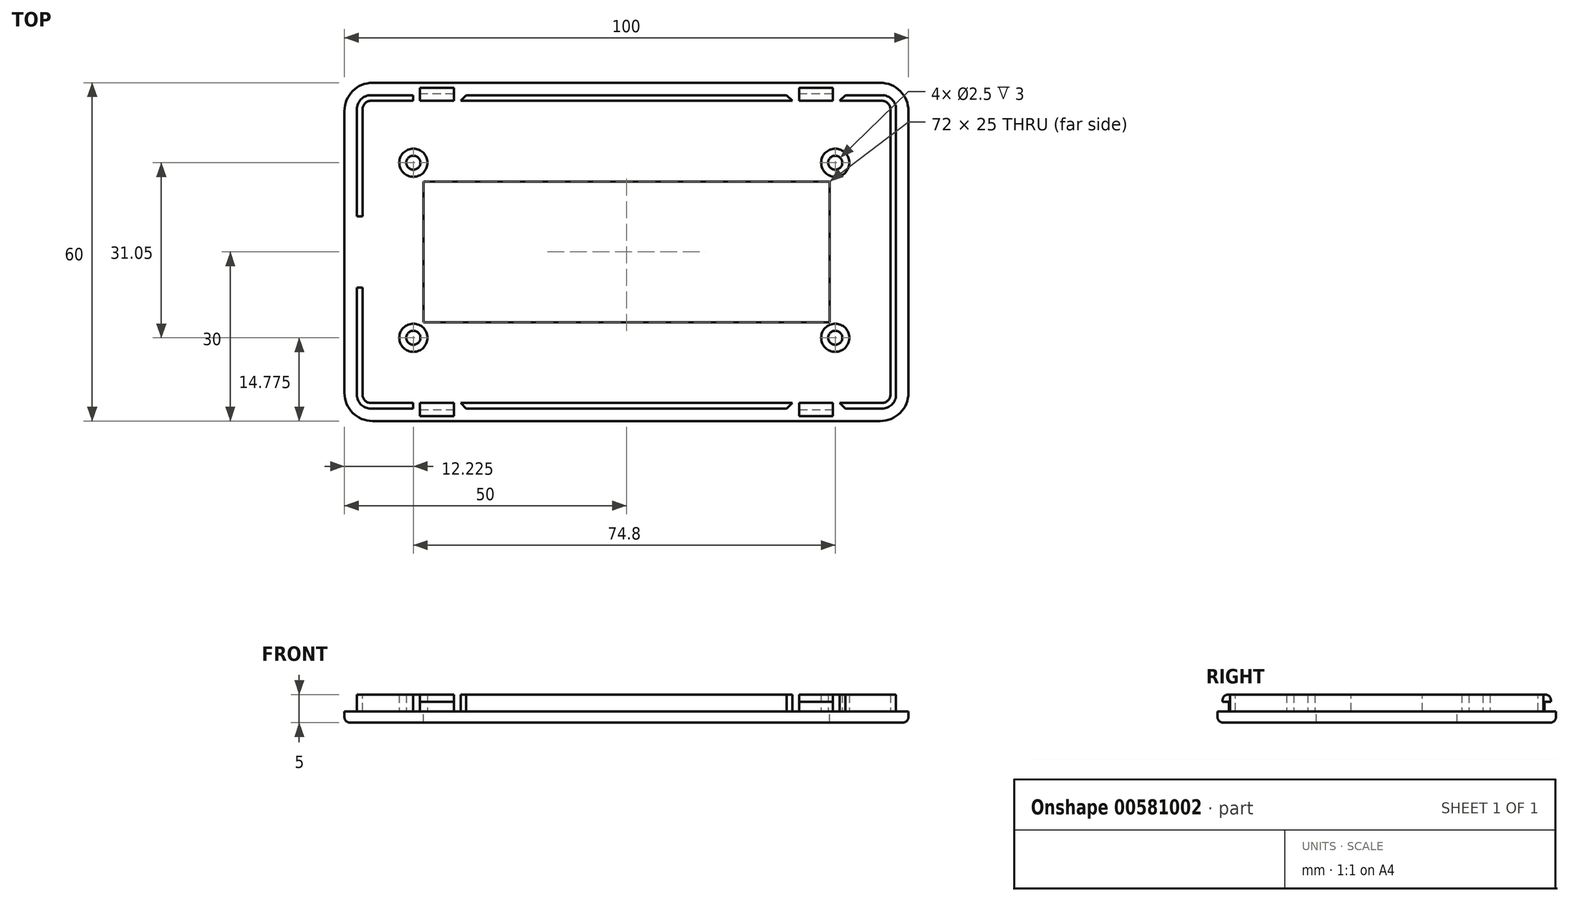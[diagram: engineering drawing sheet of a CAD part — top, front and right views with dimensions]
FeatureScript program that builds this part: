
annotation { "Feature Type Name" : "Feature", "Feature Type Description" : "" }
export const myFeature = defineFeature(function(context is Context, id is Id, definition is map)
    precondition{}
    {
        {
            var Q0;
            Q0=qCreatedBy(makeId("Top.planeOp"),FACE);
            var sketch = newSketch(context, id + "F0", { "sketchPlane" : qUnion([Q0])});
            skLineSegment(sketch, "E0.bottom", {"start": v(5, 0) * mm, "end": v(95, 0) * mm});
            skLineSegment(sketch, "E0.left", {"start": v(0, 5) * mm, "end": v(0, 30) * mm});
            skLineSegment(sketch, "E0.right", {"start": v(100, 5) * mm, "end": v(100, 30) * mm});
            skLineSegment(sketch, "E1.top", {"start": v(4.7, 2.2) * mm, "end": v(95.3, 2.2) * mm});
            skLineSegment(sketch, "E1.left", {"start": v(2.2, 30) * mm, "end": v(2.2, 4.7) * mm});
            skLineSegment(sketch, "E1.right", {"start": v(97.8, 30) * mm, "end": v(97.8, 4.7) * mm});
            skPoint(sketch, "E2.visualSharp", {"position": v(0, 0) * mm});
            skArc(sketch, "E2.filletArc", {"start": v(0, 5) * mm, "mid": v(1.46, 1.46) * mm, "end": v(5, 0) * mm});
            skPoint(sketch, "E3.visualSharp", {"position": v(100, 0) * mm});
            skArc(sketch, "E3.filletArc", {"start": v(95, 0) * mm, "mid": v(98.54, 1.46) * mm, "end": v(100, 5) * mm});
            skPoint(sketch, "E4.visualSharp", {"position": v(97.8, 2.2) * mm});
            skArc(sketch, "E4.filletArc", {"start": v(95.3, 2.2) * mm, "mid": v(97.07, 2.93) * mm, "end": v(97.8, 4.7) * mm});
            skPoint(sketch, "E5.visualSharp", {"position": v(2.2, 2.2) * mm});
            skArc(sketch, "E5.filletArc", {"start": v(2.2, 4.7) * mm, "mid": v(2.93, 2.93) * mm, "end": v(4.7, 2.2) * mm});
            skLineSegment(sketch, "E6.1", {"start": v(3.2, 30) * mm, "end": v(3.2, 4.7) * mm});
            skLineSegment(sketch, "E6.2", {"start": v(4.7, 3.2) * mm, "end": v(95.3, 3.2) * mm});
            skLineSegment(sketch, "E6.3", {"start": v(96.8, 30) * mm, "end": v(96.8, 4.7) * mm});
            skPoint(sketch, "E7.visualSharp", {"position": v(96.8, 3.2) * mm});
            skArc(sketch, "E7.filletArc", {"start": v(95.3, 3.2) * mm, "mid": v(96.36, 3.64) * mm, "end": v(96.8, 4.7) * mm});
            skPoint(sketch, "E8.visualSharp", {"position": v(3.2, 3.2) * mm});
            skArc(sketch, "E8.filletArc", {"start": v(3.2, 4.7) * mm, "mid": v(3.64, 3.64) * mm, "end": v(4.7, 3.2) * mm});
            skLineSegment(sketch, "E9", {"start": v(0, 30) * mm, "end": v(100, 30) * mm});
            skSolve(sketch);
        }
        {
            var Q0;
            Q0 = qSketchRegion(id + "F0", true);
            var Q1;
            Q1=makeQuery(id+"F0.imprint","IMPRINT",FACE,{"disambiguationData":[TD([[makeQuery(id+"F0.imprint","IMPRINT",EDGE,{"derivedFrom":sQuery(id+"F0.wireOp",EDGE,"E6.0")}),-1.0]])]});
            var Q2;
            Q2=makeQuery(id+"F0.imprint","IMPRINT",FACE,{"disambiguationData":[TD([[makeQuery(id+"F0.imprint","IMPRINT",EDGE,{"derivedFrom":sQuery(id+"F0.wireOp",EDGE,"E1.bottom")}),-1.0]])]});
            extrude(context, id + "F1", {"entities" : qUnion([Q0, Q1, Q2]), "depth" : 2 * mm, "offsetDistance" : 25 * mm});
        }
        {
            var Q0;
            Q0=makeQuery(id+"F0.imprint","IMPRINT",FACE,{"disambiguationData":[TD([[makeQuery(id+"F0.imprint","IMPRINT",EDGE,{"derivedFrom":sQuery(id+"F0.wireOp",EDGE,"E1.top")}),1.0]])]});
            extrude(context, id + "F2", {"entities" : qUnion([Q0]), "operationType" : NewBodyOperationType.ADD, "depth" : 5 * mm, "offsetDistance" : 25 * mm});
        }
        {
            var Q0;
            Q0=makeQuery(id+"F2.opExtrude","CAP_FACE",FACE,{"disambiguationData":[OSD([sQuery(id+"F0.wireOp",EDGE,"E1.top"),sQuery(id+"F0.wireOp",EDGE,"E1.left"),sQuery(id+"F0.wireOp",EDGE,"E1.right"),sQuery(id+"F0.wireOp",EDGE,"E4.filletArc"),sQuery(id+"F0.wireOp",EDGE,"E5.filletArc"),sQuery(id+"F0.wireOp",EDGE,"E6.1"),sQuery(id+"F0.wireOp",EDGE,"E6.2"),sQuery(id+"F0.wireOp",EDGE,"E6.3"),sQuery(id+"F0.wireOp",EDGE,"E7.filletArc"),sQuery(id+"F0.wireOp",EDGE,"E8.filletArc"),sQuery(id+"F0.wireOp",EDGE,"E9")])],"isStart":false});
            var sketch = newSketch(context, id + "F3", { "sketchPlane" : qUnion([Q0])});
            skLineSegment(sketch, "E10.bottom", {"start": v(2.2, 30) * mm, "end": v(3.2, 30) * mm});
            skLineSegment(sketch, "E10.top", {"start": v(2.2, 23.7) * mm, "end": v(3.2, 23.7) * mm});
            skLineSegment(sketch, "E10.left", {"start": v(2.2, 30) * mm, "end": v(2.2, 23.7) * mm});
            skLineSegment(sketch, "E10.right", {"start": v(3.2, 30) * mm, "end": v(3.2, 23.7) * mm});
            skLineSegment(sketch, "E11.bottom", {"start": v(12.2, 3.2) * mm, "end": v(13.4, 3.2) * mm});
            skLineSegment(sketch, "E11.top", {"start": v(12.2, 2.2) * mm, "end": v(13.4, 2.2) * mm});
            skLineSegment(sketch, "E11.left", {"start": v(12.2, 3.2) * mm, "end": v(12.2, 2.2) * mm});
            skLineSegment(sketch, "E11.right", {"start": v(13.4, 3.2) * mm, "end": v(13.4, 2.2) * mm});
            skLineSegment(sketch, "E12.bottom", {"start": v(86.6, 3.2) * mm, "end": v(87.8, 3.2) * mm});
            skLineSegment(sketch, "E12.top", {"start": v(86.6, 2.2) * mm, "end": v(87.8, 2.2) * mm});
            skLineSegment(sketch, "E12.left", {"start": v(86.6, 3.2) * mm, "end": v(86.6, 2.2) * mm});
            skLineSegment(sketch, "E12.right", {"start": v(87.8, 3.2) * mm, "end": v(87.8, 2.2) * mm});
            skLineSegment(sketch, "E13.bottom", {"start": v(19.4, 3.2) * mm, "end": v(20.6, 3.2) * mm});
            skLineSegment(sketch, "E13.top", {"start": v(19.4, 2.2) * mm, "end": v(20.6, 2.2) * mm});
            skLineSegment(sketch, "E13.left", {"start": v(19.4, 3.2) * mm, "end": v(19.4, 2.2) * mm});
            skLineSegment(sketch, "E13.right", {"start": v(20.6, 3.2) * mm, "end": v(20.6, 2.2) * mm});
            skLineSegment(sketch, "E14.bottom", {"start": v(80.6, 3.2) * mm, "end": v(79.4, 3.2) * mm});
            skLineSegment(sketch, "E14.top", {"start": v(80.6, 2.2) * mm, "end": v(79.4, 2.2) * mm});
            skLineSegment(sketch, "E14.left", {"start": v(80.6, 3.2) * mm, "end": v(80.6, 2.2) * mm});
            skLineSegment(sketch, "E14.right", {"start": v(79.4, 3.2) * mm, "end": v(79.4, 2.2) * mm});
            skSolve(sketch);
        }
        {
            var Q0;
            Q0=makeQuery(id+"F3.imprint","IMPRINT",FACE,{"disambiguationData":[TD([[makeQuery(id+"F3.imprint","IMPRINT",EDGE,{"derivedFrom":sQuery(id+"F3.wireOp",EDGE,"E10.bottom")}),-1.0]])]});
            var Q1;
            Q1=makeQuery(id+"F3.imprint","IMPRINT",FACE,{"disambiguationData":[TD([[makeQuery(id+"F3.imprint","IMPRINT",EDGE,{"derivedFrom":sQuery(id+"F3.wireOp",EDGE,"E11.bottom")}),-1.0]])]});
            var Q2;
            Q2=makeQuery(id+"F3.imprint","IMPRINT",FACE,{"disambiguationData":[TD([[makeQuery(id+"F3.imprint","IMPRINT",EDGE,{"derivedFrom":sQuery(id+"F3.wireOp",EDGE,"E13.bottom")}),-1.0]])]});
            var Q3;
            Q3=makeQuery(id+"F3.imprint","IMPRINT",FACE,{"disambiguationData":[TD([[makeQuery(id+"F3.imprint","IMPRINT",EDGE,{"derivedFrom":sQuery(id+"F3.wireOp",EDGE,"E14.bottom")}),-1.0]])]});
            var Q4;
            Q4=makeQuery(id+"F3.imprint","IMPRINT",FACE,{"disambiguationData":[TD([[makeQuery(id+"F3.imprint","IMPRINT",EDGE,{"derivedFrom":sQuery(id+"F3.wireOp",EDGE,"E12.bottom")}),-1.0]])]});
            extrude(context, id + "F4", {"entities" : qUnion([Q0, Q1, Q2, Q3, Q4]), "operationType" : NewBodyOperationType.REMOVE, "oppositeDirection" : true, "depth" : 3 * mm, "offsetDistance" : 25 * mm});
        }
        {
            var Q0;
            {var subQ0=sQuery(id+"F3.wireOp",EDGE,"E11.right");var subQ2=sQuery(id+"F0.wireOp",EDGE,"E1.top");Q0=makeQuery(id+"F4.boolean.opBoolean","SPLIT",FACE,{"disambiguationData":[TD([makeQuery(id+"F4.opExtrude","SWEPT_FACE",FACE,{"disambiguationData":[OSD([subQ0])]})])],"derivedFrom":makeQuery(id+"F2.opExtrude","SWEPT_FACE",FACE,{"disambiguationData":[OSD([subQ2])]})});}
            var Q1;
            {var subQ1=sQuery(id+"F0.wireOp",EDGE,"E1.top");var subQ3=sQuery(id+"F3.wireOp",EDGE,"E12.left");Q1=makeQuery(id+"F4.boolean.opBoolean","SPLIT",FACE,{"disambiguationData":[TD([makeQuery(id+"F4.opExtrude","SWEPT_FACE",FACE,{"disambiguationData":[OSD([subQ3])]})])],"derivedFrom":makeQuery(id+"F2.opExtrude","SWEPT_FACE",FACE,{"disambiguationData":[OSD([subQ1])]})});}
            extrude(context, id + "F5", {"entities" : qUnion([Q0, Q1]), "operationType" : NewBodyOperationType.ADD, "depth" : 0.2 * mm, "offsetDistance" : 25 * mm});
        }
        {
            var Q0;
            {var subQ0=sQuery(id+"F3.wireOp",EDGE,"E11.right");var subQ2=sQuery(id+"F0.wireOp",EDGE,"E1.top");Q0=makeQuery(id+"F5.opExtrude","CAP_FACE",FACE,{"disambiguationData":[OSD([subQ2]),TDD([makeQuery(id+"F4.boolean.opBoolean","SPLIT",FACE,{"disambiguationData":[TD([makeQuery(id+"F4.opExtrude","SWEPT_FACE",FACE,{"disambiguationData":[OSD([subQ0])]})])],"derivedFrom":makeQuery(id+"F2.opExtrude","SWEPT_FACE",FACE,{"disambiguationData":[OSD([subQ2])]})})])],"isStart":false});}
            var sketch = newSketch(context, id + "F6", { "sketchPlane" : qUnion([Q0])});
            skLineSegment(sketch, "E15.bottom", {"start": v(13.4, 5) * mm, "end": v(19.4, 5) * mm});
            skLineSegment(sketch, "E15.top", {"start": v(13.4, 3.7) * mm, "end": v(19.4, 3.7) * mm});
            skLineSegment(sketch, "E15.left", {"start": v(13.4, 5) * mm, "end": v(13.4, 3.7) * mm});
            skLineSegment(sketch, "E15.right", {"start": v(19.4, 5) * mm, "end": v(19.4, 3.7) * mm});
            skSolve(sketch);
        }
        {
            var Q0;
            {var subQ1=sQuery(id+"F0.wireOp",EDGE,"E1.top");var subQ3=sQuery(id+"F3.wireOp",EDGE,"E12.left");Q0=makeQuery(id+"F5.opExtrude","CAP_FACE",FACE,{"disambiguationData":[OSD([subQ1]),TDD([makeQuery(id+"F4.boolean.opBoolean","SPLIT",FACE,{"disambiguationData":[TD([makeQuery(id+"F4.opExtrude","SWEPT_FACE",FACE,{"disambiguationData":[OSD([subQ3])]})])],"derivedFrom":makeQuery(id+"F2.opExtrude","SWEPT_FACE",FACE,{"disambiguationData":[OSD([subQ1])]})})])],"isStart":false});}
            var sketch = newSketch(context, id + "F7", { "sketchPlane" : qUnion([Q0])});
            skLineSegment(sketch, "E16.bottom", {"start": v(80.6, 5) * mm, "end": v(86.6, 5) * mm});
            skLineSegment(sketch, "E16.top", {"start": v(80.6, 3.7) * mm, "end": v(86.6, 3.7) * mm});
            skLineSegment(sketch, "E16.left", {"start": v(80.6, 5) * mm, "end": v(80.6, 3.7) * mm});
            skLineSegment(sketch, "E16.right", {"start": v(86.6, 5) * mm, "end": v(86.6, 3.7) * mm});
            skSolve(sketch);
        }
        {
            var Q0;
            Q0=makeQuery(id+"F6.imprint","IMPRINT",FACE,{"disambiguationData":[TD([[makeQuery(id+"F6.imprint","IMPRINT",EDGE,{"derivedFrom":sQuery(id+"F6.wireOp",EDGE,"E15.bottom")}),-1.0]])]});
            var Q1;
            Q1=makeQuery(id+"F7.imprint","IMPRINT",FACE,{"disambiguationData":[TD([[makeQuery(id+"F7.imprint","IMPRINT",EDGE,{"derivedFrom":sQuery(id+"F7.wireOp",EDGE,"E16.bottom")}),-1.0]])]});
            extrude(context, id + "F8", {"entities" : qUnion([Q0, Q1]), "operationType" : NewBodyOperationType.ADD, "depth" : 1.1 * mm, "offsetDistance" : 25 * mm});
        }
        {
            var Q0;
            Q0=makeQuery(id+"F8.opExtrude","CAP_EDGE",EDGE,{"disambiguationData":[OSD([sQuery(id+"F6.wireOp",EDGE,"E15.bottom")])],"isStart":false});
            var Q1;
            Q1=makeQuery(id+"F8.opExtrude","CAP_EDGE",EDGE,{"disambiguationData":[OSD([sQuery(id+"F7.wireOp",EDGE,"E16.bottom")])],"isStart":false});
            fillet(context, id + "F9", {"entities" : qUnion([Q0, Q1]), "radius" : 1 * mm, "tangentPropagation" : true, "allowEdgeOverflow" : false});
        }
        {
            var Q0;
            Q0=makeQuery(id+"F4.boolean.opBoolean","COPY",EDGE,{"derivedFrom":makeQuery(id+"F4.opExtrude","SWEPT_EDGE",EDGE,{"disambiguationData":[OSD([sQuery(id+"F0.wireOp",EDGE,"E1.top"),sQuery(id+"F3.wireOp",EDGE,"E13.top"),sQuery(id+"F3.wireOp",EDGE,"E13.right")])]})});
            var Q1;
            Q1=makeQuery(id+"F4.boolean.opBoolean","COPY",EDGE,{"derivedFrom":makeQuery(id+"F4.opExtrude","SWEPT_EDGE",EDGE,{"disambiguationData":[OSD([sQuery(id+"F0.wireOp",EDGE,"E1.top"),sQuery(id+"F3.wireOp",EDGE,"E11.top"),sQuery(id+"F3.wireOp",EDGE,"E11.left")])]})});
            var Q2;
            Q2=makeQuery(id+"F4.boolean.opBoolean","COPY",EDGE,{"derivedFrom":makeQuery(id+"F4.opExtrude","SWEPT_EDGE",EDGE,{"disambiguationData":[OSD([sQuery(id+"F0.wireOp",EDGE,"E1.top"),sQuery(id+"F3.wireOp",EDGE,"E14.top"),sQuery(id+"F3.wireOp",EDGE,"E14.right")])]})});
            var Q3;
            Q3=makeQuery(id+"F4.boolean.opBoolean","COPY",EDGE,{"derivedFrom":makeQuery(id+"F4.opExtrude","SWEPT_EDGE",EDGE,{"disambiguationData":[OSD([sQuery(id+"F0.wireOp",EDGE,"E1.top"),sQuery(id+"F3.wireOp",EDGE,"E12.top"),sQuery(id+"F3.wireOp",EDGE,"E12.right")])]})});
            var Q4;
            Q4=makeQuery(id+"F4.boolean.opBoolean","COPY",EDGE,{"derivedFrom":makeQuery(id+"F4.opExtrude","SWEPT_EDGE",EDGE,{"disambiguationData":[OSD([sQuery(id+"F0.wireOp",EDGE,"E1.left"),sQuery(id+"F3.wireOp",EDGE,"E10.top"),sQuery(id+"F3.wireOp",EDGE,"E10.left")])]})});
            chamfer(context, id + "F10", {"entities" : qUnion([Q0, Q1, Q2, Q3, Q4]), "width" : 1 * mm, "tangentPropagation" : true});
        }
        {
            var Q0;
            {var subQ2=sQuery(id+"F0.wireOp",EDGE,"E9");var subQ4=sQuery(id+"F0.wireOp",EDGE,"E3.filletArc");var subQ5=sQuery(id+"F0.wireOp",EDGE,"E0.bottom");var subQ6=sQuery(id+"F0.wireOp",EDGE,"E2.filletArc");var subQ7=sQuery(id+"F0.wireOp",EDGE,"E0.left");var subQ8=sQuery(id+"F0.wireOp",EDGE,"E0.right");var subQ9=sQuery(id+"F0.wireOp",EDGE,"E6.1");var subQ13=makeQuery(id+"F1.opExtrude","CAP_FACE",FACE,{"disambiguationData":[OSD([subQ5,subQ7,subQ8,subQ6,subQ4,subQ2])],"isStart":false});Q0=makeQuery(id+"F4.boolean.opBoolean","MERGE",FACE,{"derivedFrom":[makeQuery(id+"F2.boolean.opBoolean","SPLIT",FACE,{"disambiguationData":[TD([makeQuery(id+"F2.opExtrude","SWEPT_FACE",FACE,{"disambiguationData":[OSD([subQ9])]})])],"derivedFrom":subQ13}),makeQuery(id+"F2.boolean.opBoolean","SPLIT",FACE,{"disambiguationData":[TD([makeQuery(id+"F1.opExtrude","SWEPT_FACE",FACE,{"disambiguationData":[OSD([subQ5])]})])],"derivedFrom":subQ13}),makeQuery(id+"F4.opExtrude","CAP_FACE",FACE,{"disambiguationData":[OSD([sQuery(id+"F3.wireOp",EDGE,"E10.bottom"),sQuery(id+"F3.wireOp",EDGE,"E10.top"),sQuery(id+"F3.wireOp",EDGE,"E10.left"),sQuery(id+"F3.wireOp",EDGE,"E10.right")])],"isStart":false}),makeQuery(id+"F4.opExtrude","CAP_FACE",FACE,{"disambiguationData":[OSD([sQuery(id+"F3.wireOp",EDGE,"E11.bottom"),sQuery(id+"F3.wireOp",EDGE,"E11.top"),sQuery(id+"F3.wireOp",EDGE,"E11.left"),sQuery(id+"F3.wireOp",EDGE,"E11.right")])],"isStart":false}),makeQuery(id+"F4.opExtrude","CAP_FACE",FACE,{"disambiguationData":[OSD([sQuery(id+"F3.wireOp",EDGE,"E12.bottom"),sQuery(id+"F3.wireOp",EDGE,"E12.top"),sQuery(id+"F3.wireOp",EDGE,"E12.left"),sQuery(id+"F3.wireOp",EDGE,"E12.right")])],"isStart":false}),makeQuery(id+"F4.opExtrude","CAP_FACE",FACE,{"disambiguationData":[OSD([sQuery(id+"F3.wireOp",EDGE,"E13.bottom"),sQuery(id+"F3.wireOp",EDGE,"E13.top"),sQuery(id+"F3.wireOp",EDGE,"E13.left"),sQuery(id+"F3.wireOp",EDGE,"E13.right")])],"isStart":false}),makeQuery(id+"F4.opExtrude","CAP_FACE",FACE,{"disambiguationData":[OSD([sQuery(id+"F3.wireOp",EDGE,"E14.bottom"),sQuery(id+"F3.wireOp",EDGE,"E14.top"),sQuery(id+"F3.wireOp",EDGE,"E14.left"),sQuery(id+"F3.wireOp",EDGE,"E14.right")])],"isStart":false})]});}
            var sketch = newSketch(context, id + "F11", { "sketchPlane" : qUnion([Q0])});
            skLineSegment(sketch, "E17.bottom", {"start": v(86, 17.5) * mm, "end": v(14, 17.5) * mm});
            skLineSegment(sketch, "E17.top", {"start": v(86, 42.5) * mm, "end": v(14, 42.5) * mm});
            skLineSegment(sketch, "E17.left", {"start": v(86, 17.5) * mm, "end": v(86, 42.5) * mm});
            skLineSegment(sketch, "E17.right", {"start": v(14, 17.5) * mm, "end": v(14, 42.5) * mm});
            skPoint(sketch, "E17.middle", {"position": v(50, 30) * mm});
            skSolve(sketch);
        }
        {
            var Q0;
            {var subQ0=sQuery(id+"F11.wireOp",EDGE,"E17.bottom");Q0=makeQuery(id+"F11.imprint","IMPRINT",FACE,{"disambiguationData":[TD([[makeQuery(id+"F11.imprint","IMPRINT",EDGE,{"derivedFrom":subQ0}),-1.0]])]});}
            extrude(context, id + "F12", {"entities" : qUnion([Q0]), "operationType" : NewBodyOperationType.REMOVE, "endBound" : BoundingType.UP_TO_NEXT, "oppositeDirection" : true, "depth" : 25 * mm, "offsetDistance" : 25 * mm});
        }
        {
            var Q0;
            Q0=makeQuery(id+"F1.opExtrude","CAP_EDGE",EDGE,{"disambiguationData":[OSD([sQuery(id+"F0.wireOp",EDGE,"E0.bottom")])],"isStart":true});
            fillet(context, id + "F13", {"entities" : qUnion([Q0]), "radius" : 1 * mm, "tangentPropagation" : true, "allowEdgeOverflow" : false});
        }
        {
            var Q0;
            Q0=makeQuery(id+"F1.opExtrude","SWEPT_BODY",BODY,{"disambiguationData":[OSD([sQuery(id+"F0.wireOp",EDGE,"E0.bottom"),sQuery(id+"F0.wireOp",EDGE,"E0.left"),sQuery(id+"F0.wireOp",EDGE,"E0.right"),sQuery(id+"F0.wireOp",EDGE,"E2.filletArc"),sQuery(id+"F0.wireOp",EDGE,"E3.filletArc"),sQuery(id+"F0.wireOp",EDGE,"E9")])]});
            var Q1;
            {var subQ0=sQuery(id+"F0.wireOp",EDGE,"E0.left");var subQ1=sQuery(id+"F0.wireOp",EDGE,"E9");Q1=makeQuery(id+"F12.boolean.opBoolean","SPLIT",FACE,{"disambiguationData":[TD([makeQuery(id+"F1.opExtrude","SWEPT_FACE",FACE,{"disambiguationData":[OSD([subQ0])]})])],"derivedFrom":makeQuery(id+"F2.boolean.opBoolean","MERGE",FACE,{"derivedFrom":[makeQuery(id+"F1.opExtrude","SWEPT_FACE",FACE,{"disambiguationData":[OSD([subQ1])]}),makeQuery(id+"F2.opExtrude","SWEPT_FACE",FACE,{"disambiguationData":[OSD([subQ1]),TDD([makeQuery(id+"F0.imprint","IMPRINT",EDGE,{"disambiguationData":[TD([[makeQuery(id+"F0.imprint","INTERSECT",VERTEX,{"derivedFrom":[sQuery(id+"F0.wireOp",EDGE,"E1.left"),subQ1]}),-1.0]])],"derivedFrom":subQ1})])]}),makeQuery(id+"F2.opExtrude","SWEPT_FACE",FACE,{"disambiguationData":[OSD([subQ1]),TDD([makeQuery(id+"F0.imprint","IMPRINT",EDGE,{"disambiguationData":[TD([[makeQuery(id+"F0.imprint","INTERSECT",VERTEX,{"derivedFrom":[sQuery(id+"F0.wireOp",EDGE,"E1.right"),subQ1]}),1.0]])],"derivedFrom":subQ1})])]})]})});}
            mirror(context, id + "F14", {"operationType" : NewBodyOperationType.ADD, "entities" : qUnion([Q0]), "mirrorPlane" : qUnion([Q1])});
        }
        {
            var Q0;
            {var subQ2=sQuery(id+"F0.wireOp",EDGE,"E9");var subQ4=sQuery(id+"F0.wireOp",EDGE,"E3.filletArc");var subQ5=sQuery(id+"F0.wireOp",EDGE,"E0.bottom");var subQ6=sQuery(id+"F0.wireOp",EDGE,"E2.filletArc");var subQ7=sQuery(id+"F0.wireOp",EDGE,"E0.left");var subQ8=sQuery(id+"F0.wireOp",EDGE,"E0.right");var subQ9=sQuery(id+"F0.wireOp",EDGE,"E6.1");var subQ13=makeQuery(id+"F1.opExtrude","CAP_FACE",FACE,{"disambiguationData":[OSD([subQ5,subQ7,subQ8,subQ6,subQ4,subQ2])],"isStart":false});var subQ14=makeQuery(id+"F4.boolean.opBoolean","MERGE",FACE,{"derivedFrom":[makeQuery(id+"F2.boolean.opBoolean","SPLIT",FACE,{"disambiguationData":[TD([makeQuery(id+"F2.opExtrude","SWEPT_FACE",FACE,{"disambiguationData":[OSD([subQ9])]})])],"derivedFrom":subQ13}),makeQuery(id+"F2.boolean.opBoolean","SPLIT",FACE,{"disambiguationData":[TD([makeQuery(id+"F1.opExtrude","SWEPT_FACE",FACE,{"disambiguationData":[OSD([subQ5])]})])],"derivedFrom":subQ13}),makeQuery(id+"F4.opExtrude","CAP_FACE",FACE,{"disambiguationData":[OSD([sQuery(id+"F3.wireOp",EDGE,"E10.bottom"),sQuery(id+"F3.wireOp",EDGE,"E10.top"),sQuery(id+"F3.wireOp",EDGE,"E10.left"),sQuery(id+"F3.wireOp",EDGE,"E10.right")])],"isStart":false}),makeQuery(id+"F4.opExtrude","CAP_FACE",FACE,{"disambiguationData":[OSD([sQuery(id+"F3.wireOp",EDGE,"E11.bottom"),sQuery(id+"F3.wireOp",EDGE,"E11.top"),sQuery(id+"F3.wireOp",EDGE,"E11.left"),sQuery(id+"F3.wireOp",EDGE,"E11.right")])],"isStart":false}),makeQuery(id+"F4.opExtrude","CAP_FACE",FACE,{"disambiguationData":[OSD([sQuery(id+"F3.wireOp",EDGE,"E12.bottom"),sQuery(id+"F3.wireOp",EDGE,"E12.top"),sQuery(id+"F3.wireOp",EDGE,"E12.left"),sQuery(id+"F3.wireOp",EDGE,"E12.right")])],"isStart":false}),makeQuery(id+"F4.opExtrude","CAP_FACE",FACE,{"disambiguationData":[OSD([sQuery(id+"F3.wireOp",EDGE,"E13.bottom"),sQuery(id+"F3.wireOp",EDGE,"E13.top"),sQuery(id+"F3.wireOp",EDGE,"E13.left"),sQuery(id+"F3.wireOp",EDGE,"E13.right")])],"isStart":false}),makeQuery(id+"F4.opExtrude","CAP_FACE",FACE,{"disambiguationData":[OSD([sQuery(id+"F3.wireOp",EDGE,"E14.bottom"),sQuery(id+"F3.wireOp",EDGE,"E14.top"),sQuery(id+"F3.wireOp",EDGE,"E14.left"),sQuery(id+"F3.wireOp",EDGE,"E14.right")])],"isStart":false})]});Q0=makeQuery(id+"F14.boolean.opBoolean","MERGE",FACE,{"derivedFrom":[subQ14,makeQuery(id+"F14.opPattern","COPY",FACE,{"derivedFrom":subQ14,"instanceName":"1"})]});}
            var sketch = newSketch(context, id + "F15", { "sketchPlane" : qUnion([Q0])});
            skCircle(sketch, "E18", {"center": v(12.22, 45.83) * mm, "radius": 1.25 * mm});
            skCircle(sketch, "E19", {"center": v(87.03, 45.83) * mm, "radius": 1.25 * mm});
            skCircle(sketch, "E20", {"center": v(87.03, 14.78) * mm, "radius": 1.25 * mm});
            skCircle(sketch, "E21", {"center": v(12.22, 14.78) * mm, "radius": 1.25 * mm});
            skCircle(sketch, "E22", {"center": v(12.22, 45.83) * mm, "radius": 2.5 * mm});
            skCircle(sketch, "E23", {"center": v(87.03, 45.83) * mm, "radius": 2.5 * mm});
            skCircle(sketch, "E24", {"center": v(87.03, 14.78) * mm, "radius": 2.5 * mm});
            skCircle(sketch, "E25", {"center": v(12.22, 14.78) * mm, "radius": 2.5 * mm});
            skSolve(sketch);
        }
        {
            var Q0;
            Q0 = qSketchRegion(id + "F15", true);
            extrude(context, id + "F16", {"entities" : qUnion([Q0]), "operationType" : NewBodyOperationType.ADD, "depth" : 3 * mm, "offsetDistance" : 25 * mm});
        }
    });
